# Revit family: Door_BiFold_Dunbarton_4-Panel-Mirror
name_source: partatom
category: Doors
units: mm (PartAtom-declared; Revit-internal decimal feet)

## family parameters
Always vertical = Yes
Classification Number = 23.30.10.17.17
Cut with Voids When Loaded = No
Host = Wall
Room Calculation Point = No
Shared = No

## types (1)
- Type as Specified
    Air Infiltration = as Specified
    Assembly Code = C1020100
    Description = Dunbarton Four-Panel Bifold Mirror Door - Type as Specified
    Door Panel Type = as Specified
    Door Thickness = 0' - 1 1/4"
    Expected Lifespan (Years) = 0
    Fire Rating = as Specified
    Frame Thickness = 0' - 0 5/8"
    Function = Interior
    Green Building-LEED = http://www.arcat.com
    Impact Resistance = as Specified
    Installation-Fabrication = https://dunbarton.com
    Keynote = 08 11 10
    Maintenance Schedule (Months) = 0
    Manufacturer = Dunbarton Corporation
    Manufacturer Fax = 334-793-7022
    Manufacturer Website = https://dunbarton.com
    Model = as Specified
    Opening Height = 6' - 8"
    Panel_Framed = Yes
    Panel_Frameless = No
    Product Data = http://www.arcat.com
    Product Properties = https://dunbarton.com
    R-Value = 0
    RO Spacing Sides = 0' - 0"
    RO Spacing Top = 0' - 0"
    Rough Height = 0' - 0"
    Rough Width = 0' - 0"
    Sales Information = https://dunbarton.com
    Specification = http://www.arcat.com
    Structural Test Pressure = as Specified
    Thickness = 0' - 0"
    URL = https://dunbarton.com
    Unit Width = 5' - 11"
    Wall Closure = By host
    Warranty Duration (Years) = 0
    Water Penetration = as Specified
    Width = 5' - 11"

## geometry (parser evidence)
native form markers: Sweep x10
no freeform markers — native parametric forms only
